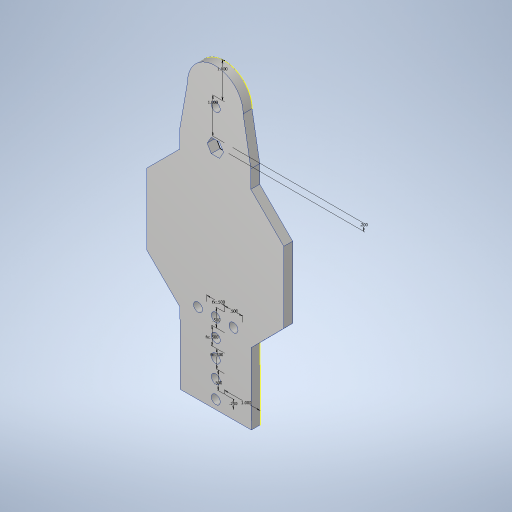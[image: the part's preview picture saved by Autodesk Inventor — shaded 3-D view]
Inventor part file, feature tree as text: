
AUTODESK INVENTOR PART (.ipt)
format: ipt  version: 2023.4 (Build 274418000, 418)  size: 304,640 bytes
history: native  units: in
note: dims shown in document units (in); Inventor stores cm internally (conversion verified against a paired STEP export)
features: extrude x2, sketch x2, hole x1
ambient origin geometry x8: Origin, YZ Plane, XZ Plane, XY Plane, X Axis, Y Axis, Z Axis, Center Point
bodies: Solid1 (feature_tree)
feature tree (5):
  extrude  "Extrusion1"  Depth=2.0in
  sketch  "Sketch2"  dims[d2=1.311in d3=1.311in d4=135.0deg d5=135.0deg d6=2.0in d7=2.0in d8=1.311in d9=1.311in d10=135.0deg d11=135.0deg d12=0.5in d13=0.5in d15=1.25in d16=1.1681in d17=1.25in d18=1.1681in d19=0.25in d20=0.0in d21=0.25in d22=1.0in d23=0.5in d24=0.5in d25=0.5in d26=0.5in d27=0.5in d28=0.5in d29=1.0in d30=0.2in d31=1.0in d32=0.25in d33=0.75in d34=0.507in d35=0.25in d36=0.5635in d37=1.0in d38=0.8108in d39=0.25in d40=0.0in]
  hole  "Hole1"  [1 undecoded]
  extrude  "Extrusion2"  TaperAngle=135.0deg  [1 undecoded]
  sketch  "Sketch1"  dims[d0=2.0in d1=2.0in]
note: 2 required parameter values undecoded (feature->parameter linkage not recoverable at this tier; creation-order binding heuristic only, values carry confidence <= 0.55)
